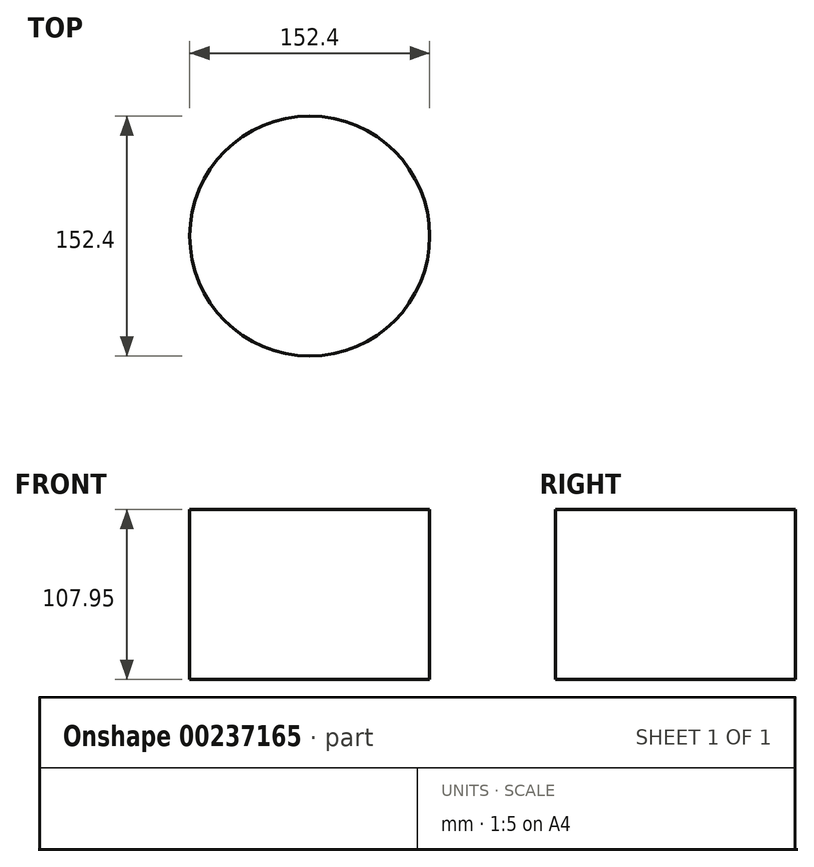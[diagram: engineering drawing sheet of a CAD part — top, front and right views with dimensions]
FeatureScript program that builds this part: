
annotation { "Feature Type Name" : "Feature", "Feature Type Description" : "" }
export const myFeature = defineFeature(function(context is Context, id is Id, definition is map)
    precondition{}
    {
        {
            var Q0;
            Q0=qCreatedBy(makeId("Top.planeOp"),FACE);
            var sketch = newSketch(context, id + "F0", { "sketchPlane" : qUnion([Q0])});
            skCircle(sketch, "E0", {"center": v(0, 0) * mm, "radius": 76.2 * mm});
            skSolve(sketch);
        }
        {
            var Q0;
            Q0 = qSketchRegion(id + "F0", true);
            extrude(context, id + "F1", {"entities" : qUnion([Q0]), "oppositeDirection" : true, "depth" : 107.95 * mm});
        }
    });
